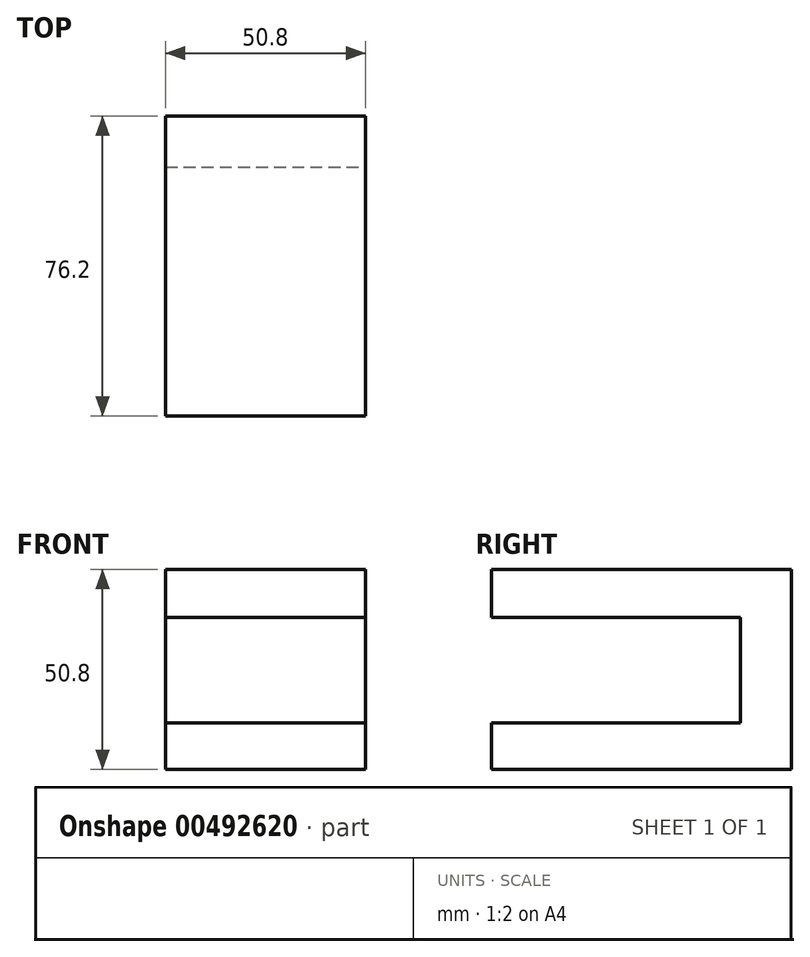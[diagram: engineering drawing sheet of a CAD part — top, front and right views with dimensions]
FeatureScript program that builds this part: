
annotation { "Feature Type Name" : "Feature", "Feature Type Description" : "" }
export const myFeature = defineFeature(function(context is Context, id is Id, definition is map)
    precondition{}
    {
        {
            var Q0;
            Q0=qCreatedBy(makeId("Front.planeOp"),FACE);
            var sketch = newSketch(context, id + "F0", { "sketchPlane" : qUnion([Q0])});
            skLineSegment(sketch, "E0.bottom", {"start": v(-4.08, -2.81) * mm, "end": v(-54.88, -2.81) * mm});
            skLineSegment(sketch, "E0.top", {"start": v(-4.08, 47.99) * mm, "end": v(-54.88, 47.99) * mm});
            skLineSegment(sketch, "E0.left", {"start": v(-4.08, -2.81) * mm, "end": v(-4.08, 47.99) * mm});
            skLineSegment(sketch, "E0.right", {"start": v(-54.88, -2.81) * mm, "end": v(-54.88, 47.99) * mm});
            skPoint(sketch, "E0.middle", {"position": v(-29.48, 22.59) * mm});
            skSolve(sketch);
        }
        {
            var Q0;
            Q0 = qSketchRegion(id + "F0", true);
            extrude(context, id + "F1", {"entities" : qUnion([Q0]), "depth" : 76.2 * mm});
        }
        {
            var Q0;
            Q0=makeQuery(id+"F1.opExtrude","SWEPT_FACE",FACE,{"disambiguationData":[OSD([sQuery(id+"F0.wireOp",EDGE,"E0.left")])]});
            var sketch = newSketch(context, id + "F2", { "sketchPlane" : qUnion([Q0])});
            skLineSegment(sketch, "E1.bottom", {"start": v(-76.2, 35.8) * mm, "end": v(-12.93, 35.8) * mm});
            skLineSegment(sketch, "E1.top", {"start": v(-76.2, 9.02) * mm, "end": v(-12.93, 9.02) * mm});
            skLineSegment(sketch, "E1.left", {"start": v(-76.2, 35.8) * mm, "end": v(-76.2, 9.02) * mm});
            skLineSegment(sketch, "E1.right", {"start": v(-12.93, 35.8) * mm, "end": v(-12.93, 9.02) * mm});
            skSolve(sketch);
        }
        {
            var Q0;
            Q0=qCreatedBy(makeId("Right.planeOp"),FACE);
            var sketch = newSketch(context, id + "F3", { "sketchPlane" : qUnion([Q0])});
            skSolve(sketch);
        }
        {
            var Q0;
            Q0 = qSketchRegion(id + "F3", true);
            var Q1;
            Q1=makeQuery(id+"F2.imprint","IMPRINT",FACE,{"disambiguationData":[TD([[makeQuery(id+"F2.imprint","IMPRINT",EDGE,{"derivedFrom":sQuery(id+"F2.wireOp",EDGE,"E1.bottom")}),-1.0]])]});
            extrude(context, id + "F4", {"entities" : qUnion([Q0, Q1]), "operationType" : NewBodyOperationType.REMOVE, "endBound" : BoundingType.THROUGH_ALL, "oppositeDirection" : true, "depth" : 25.4 * mm});
        }
    });
